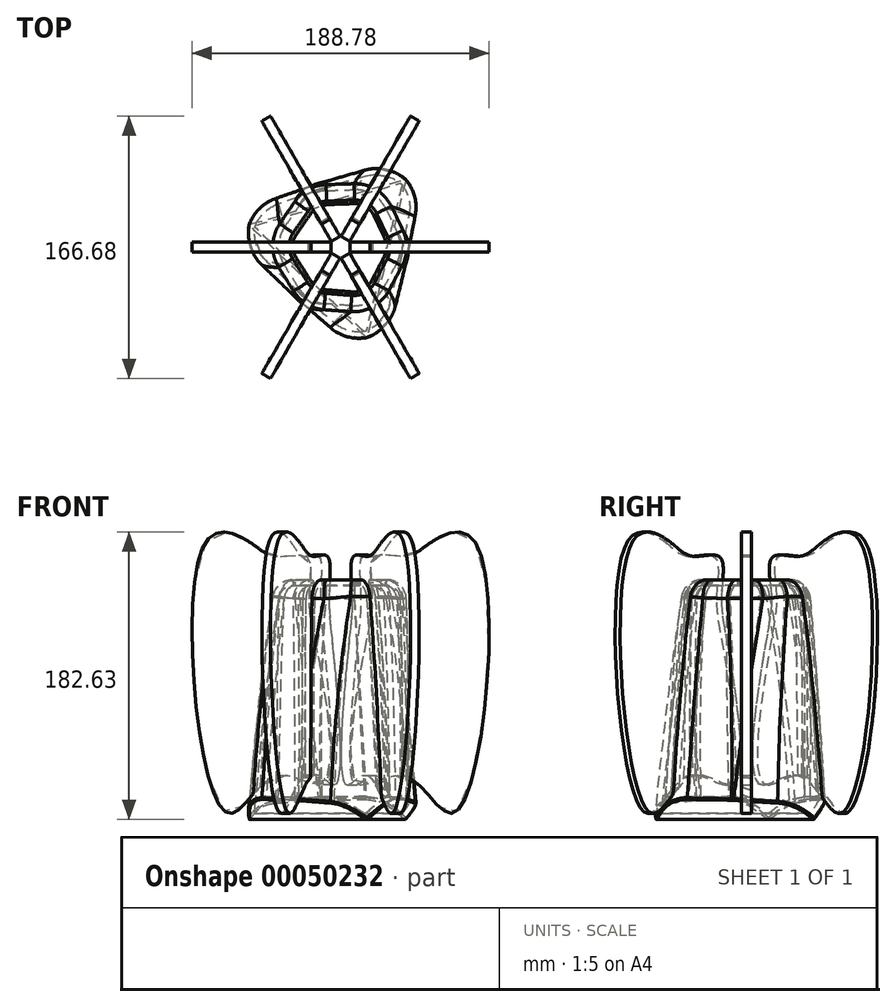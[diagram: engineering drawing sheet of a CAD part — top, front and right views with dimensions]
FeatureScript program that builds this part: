
annotation { "Feature Type Name" : "Feature", "Feature Type Description" : "" }
export const myFeature = defineFeature(function(context is Context, id is Id, definition is map)
    precondition{}
    {
        {
            var Q0;
            Q0=qCreatedBy(makeId("Top.planeOp"),FACE);
            var sketch = newSketch(context, id + "F0", { "sketchPlane" : qUnion([Q0])});
            skCircle(sketch, "E0.cCircle", {"center": v(0, 0) * mm, "radius": 42.63 * mm, "construction": true});
            skLineSegment(sketch, "E0.0", {"start": v(58, 62.5) * mm, "end": v(41.56, -9.5) * mm});
            skLineSegment(sketch, "E0.1", {"start": v(25.12, -81.48) * mm, "end": v(-29, -31.25) * mm});
            skLineSegment(sketch, "E0.2", {"start": v(-83.12, 18.99) * mm, "end": v(-12.56, 40.74) * mm});
            skPoint(sketch, "E0.0.midPoint", {"position": v(41.56, -9.5) * mm});
            skLineSegment(sketch, "E1", {"start": v(-29, -31.25) * mm, "end": v(-83.12, 18.99) * mm});
            skLineSegment(sketch, "E2", {"start": v(-12.56, 40.74) * mm, "end": v(58, 62.5) * mm});
            skLineSegment(sketch, "E3", {"start": v(41.56, -9.5) * mm, "end": v(25.12, -81.48) * mm});
            skSolve(sketch);
        }
        {
            var Q0;
            Q0=qCreatedBy(makeId("Top.planeOp"),FACE);
            cPlane(context, id + "F1", {"entities" : qUnion([Q0]), "cplaneType" : CPlaneType.OFFSET, "offset" : 152.4 * mm, "width" : 152.4 * mm, "height" : 152.4 * mm});
        }
        {
            var Q0;
            Q0=qCreatedBy(id+"F1.planeOp",FACE);
            var sketch = newSketch(context, id + "F2", { "sketchPlane" : qUnion([Q0])});
            skCircle(sketch, "E4.cCircle", {"center": v(0, 0) * mm, "radius": 39.17 * mm, "construction": true});
            skLineSegment(sketch, "E4.0", {"start": v(-22.61, 39.17) * mm, "end": v(22.61, 39.17) * mm});
            skLineSegment(sketch, "E4.1", {"start": v(22.61, 39.17) * mm, "end": v(45.23, 0) * mm});
            skLineSegment(sketch, "E4.2", {"start": v(45.23, 0) * mm, "end": v(22.61, -39.17) * mm});
            skLineSegment(sketch, "E4.3", {"start": v(22.61, -39.17) * mm, "end": v(-22.61, -39.17) * mm});
            skLineSegment(sketch, "E4.4", {"start": v(-22.61, -39.17) * mm, "end": v(-45.23, 0) * mm});
            skLineSegment(sketch, "E4.5", {"start": v(-45.23, 0) * mm, "end": v(-22.61, 39.17) * mm});
            skPoint(sketch, "E4.0.midPoint", {"position": v(0, 39.17) * mm});
            skSolve(sketch);
        }
        {
            var Q0;
            Q0=makeQuery(id+"F2.imprint","IMPRINT",FACE,{"disambiguationData":[TD([[makeQuery(id+"F2.imprint","IMPRINT",EDGE,{"derivedFrom":sQuery(id+"F2.wireOp",EDGE,"E4.0")}),-1.0]])]});
            var Q1;
            Q1=makeQuery(id+"F0.imprint","IMPRINT",FACE,{"disambiguationData":[TD([[makeQuery(id+"F0.imprint","IMPRINT",EDGE,{"derivedFrom":sQuery(id+"F0.wireOp",EDGE,"E0.0")}),-1.0]])]});
            loft(context, id + "F3", {"sheetProfilesArray" : [{ "sheetProfileEntities" : qUnion([Q0]) }, { "sheetProfileEntities" : qUnion([Q1]) }]});
        }
        {
            var Q0;
            Q0=makeQuery(id+"F3.opLoft","MID_CAP_EDGE",EDGE,{"disambiguationData":[OSD([sQuery(id+"F2.wireOp",EDGE,"E4.2"),sQuery(id+"F2.wireOp",EDGE,"E4.3"),sQuery(id+"F2.wireOp",EDGE,"E4.4")])],"capPos":0.0});
            var Q1;
            Q1=makeQuery(id+"F3.opLoft","MID_CAP_EDGE",EDGE,{"disambiguationData":[OSD([sQuery(id+"F2.wireOp",EDGE,"E4.1"),sQuery(id+"F2.wireOp",EDGE,"E4.2"),sQuery(id+"F2.wireOp",EDGE,"E4.3")])],"capPos":0.0});
            var Q2;
            Q2=makeQuery(id+"F3.opLoft","MID_CAP_EDGE",EDGE,{"disambiguationData":[OSD([sQuery(id+"F2.wireOp",EDGE,"E4.0"),sQuery(id+"F2.wireOp",EDGE,"E4.1"),sQuery(id+"F2.wireOp",EDGE,"E4.2")])],"capPos":0.0});
            var Q3;
            Q3=makeQuery(id+"F3.opLoft","MID_CAP_EDGE",EDGE,{"disambiguationData":[OSD([sQuery(id+"F2.wireOp",EDGE,"E4.0"),sQuery(id+"F2.wireOp",EDGE,"E4.1"),sQuery(id+"F2.wireOp",EDGE,"E4.5")])],"capPos":0.0});
            var Q4;
            Q4=makeQuery(id+"F3.opLoft","MID_CAP_EDGE",EDGE,{"disambiguationData":[OSD([sQuery(id+"F2.wireOp",EDGE,"E4.0"),sQuery(id+"F2.wireOp",EDGE,"E4.4"),sQuery(id+"F2.wireOp",EDGE,"E4.5")])],"capPos":0.0});
            var Q5;
            Q5=makeQuery(id+"F3.opLoft","MID_CAP_EDGE",EDGE,{"disambiguationData":[OSD([sQuery(id+"F2.wireOp",EDGE,"E4.3"),sQuery(id+"F2.wireOp",EDGE,"E4.4"),sQuery(id+"F2.wireOp",EDGE,"E4.5")])],"capPos":0.0});
            fillet(context, id + "F4", {"entities" : qUnion([Q0, Q1, Q2, Q3, Q4, Q5]), "radius" : 12.7 * mm, "tangentPropagation" : true, "allowEdgeOverflow" : false});
        }
        {
            var Q0;
            Q0=makeQuery(id+"F3.opLoft","MID_CAP_EDGE",EDGE,{"disambiguationData":[OSD([sQuery(id+"F0.wireOp",EDGE,"E0.0"),sQuery(id+"F0.wireOp",EDGE,"E0.1"),sQuery(id+"F0.wireOp",EDGE,"E3")])],"capPos":1.0});
            chamfer(context, id + "F5", {"entities" : qUnion([Q0]), "width" : 12.7 * mm, "tangentPropagation" : true});
        }
        {
            var Q0;
            Q0=makeQuery(id+"F3.opLoft","MID_CAP_EDGE",EDGE,{"disambiguationData":[OSD([sQuery(id+"F0.wireOp",EDGE,"E0.0"),sQuery(id+"F0.wireOp",EDGE,"E0.2"),sQuery(id+"F0.wireOp",EDGE,"E2")])],"capPos":1.0});
            chamfer(context, id + "F6", {"entities" : qUnion([Q0]), "width" : 12.7 * mm, "tangentPropagation" : true});
        }
        {
            var Q0;
            Q0=makeQuery(id+"F3.opLoft","MID_CAP_EDGE",EDGE,{"disambiguationData":[OSD([sQuery(id+"F0.wireOp",EDGE,"E0.1"),sQuery(id+"F0.wireOp",EDGE,"E0.2"),sQuery(id+"F0.wireOp",EDGE,"E1")])],"capPos":1.0});
            chamfer(context, id + "F7", {"entities" : qUnion([Q0]), "width" : 12.7 * mm, "tangentPropagation" : true});
        }
        {
            var Q0;
            Q0=makeQuery(id+"F3.opLoft","SWEPT_EDGE",EDGE,{"disambiguationData":[OSD([sQuery(id+"F0.wireOp",EDGE,"E0.1"),sQuery(id+"F0.wireOp",EDGE,"E3"),sQuery(id+"F2.wireOp",EDGE,"E4.2"),sQuery(id+"F2.wireOp",EDGE,"E4.3")])]});
            var Q1;
            Q1=makeQuery(id+"F3.opLoft","SWEPT_EDGE",EDGE,{"disambiguationData":[OSD([sQuery(id+"F0.wireOp",EDGE,"E0.0"),sQuery(id+"F0.wireOp",EDGE,"E3"),sQuery(id+"F2.wireOp",EDGE,"E4.1"),sQuery(id+"F2.wireOp",EDGE,"E4.2")])]});
            var Q2;
            Q2=makeQuery(id+"F3.opLoft","SWEPT_EDGE",EDGE,{"disambiguationData":[OSD([sQuery(id+"F0.wireOp",EDGE,"E0.0"),sQuery(id+"F0.wireOp",EDGE,"E2"),sQuery(id+"F2.wireOp",EDGE,"E4.0"),sQuery(id+"F2.wireOp",EDGE,"E4.1")])]});
            var Q3;
            Q3=makeQuery(id+"F3.opLoft","SWEPT_EDGE",EDGE,{"disambiguationData":[OSD([sQuery(id+"F0.wireOp",EDGE,"E0.2"),sQuery(id+"F0.wireOp",EDGE,"E2"),sQuery(id+"F2.wireOp",EDGE,"E4.0"),sQuery(id+"F2.wireOp",EDGE,"E4.5")])]});
            var Q4;
            Q4=makeQuery(id+"F3.opLoft","SWEPT_EDGE",EDGE,{"disambiguationData":[OSD([sQuery(id+"F0.wireOp",EDGE,"E0.2"),sQuery(id+"F0.wireOp",EDGE,"E1"),sQuery(id+"F2.wireOp",EDGE,"E4.4"),sQuery(id+"F2.wireOp",EDGE,"E4.5")])]});
            var Q5;
            Q5=makeQuery(id+"F3.opLoft","SWEPT_EDGE",EDGE,{"disambiguationData":[OSD([sQuery(id+"F0.wireOp",EDGE,"E0.1"),sQuery(id+"F0.wireOp",EDGE,"E1"),sQuery(id+"F2.wireOp",EDGE,"E4.3"),sQuery(id+"F2.wireOp",EDGE,"E4.4")])]});
            fillet(context, id + "F8", {"entities" : qUnion([Q0, Q1, Q2, Q3, Q4, Q5]), "radius" : 25.4 * mm, "tangentPropagation" : true, "allowEdgeOverflow" : false});
        }
        {
            var Q0;
            Q0=makeQuery(id+"F3.opLoft","CAP_FACE",FACE,{"disambiguationData":[OSD([makeQuery(id+"F2.imprint","IMPRINT",FACE,{"disambiguationData":[TD([[makeQuery(id+"F2.imprint","IMPRINT",EDGE,{"derivedFrom":sQuery(id+"F2.wireOp",EDGE,"E4.0")}),-1.0]])]})])],"isStart":true});
            shell(context, id + "F9", {"entities" : qUnion([Q0]), "thickness" : 3.8 * mm});
        }
        {
            var Q0;
            {var subQ0=sQuery(id+"F2.wireOp",EDGE,"E4.0");var subQ1=sQuery(id+"F2.wireOp",EDGE,"E4.4");var subQ2=sQuery(id+"F2.wireOp",EDGE,"E4.5");Q0=makeQuery(id+"F4.opFillet","BLEND_EDGE",EDGE,{"blendedFrom":[makeQuery(id+"F3.opLoft","MID_CAP_EDGE",EDGE,{"disambiguationData":[OSD([subQ0,subQ1,subQ2])],"capPos":0.0}),makeQuery(id+"F3.opLoft","CAP_FACE",FACE,{"disambiguationData":[OSD([makeQuery(id+"F2.imprint","IMPRINT",FACE,{"disambiguationData":[TD([[makeQuery(id+"F2.imprint","IMPRINT",EDGE,{"derivedFrom":subQ0}),-1.0]])]})])],"isStart":true})],"blendedInto":[makeQuery(id+"F3.opLoft","CAP_FACE",FACE,{"disambiguationData":[OSD([makeQuery(id+"F2.imprint","IMPRINT",FACE,{"disambiguationData":[TD([[makeQuery(id+"F2.imprint","IMPRINT",EDGE,{"derivedFrom":subQ0}),-1.0]])]})])],"isStart":true})]});}
            var Q1;
            {var subQ0=sQuery(id+"F2.wireOp",EDGE,"E4.1");var subQ1=sQuery(id+"F2.wireOp",EDGE,"E4.0");var subQ2=sQuery(id+"F2.wireOp",EDGE,"E4.4");var subQ3=sQuery(id+"F2.wireOp",EDGE,"E4.5");Q1=makeQuery(id+"F8.opFillet","BLEND_EDGE",EDGE,{"blendedFrom":[makeQuery(id+"F4.opFillet","BLEND_EDGE",EDGE,{"blendedFrom":[makeQuery(id+"F3.opLoft","MID_CAP_EDGE",EDGE,{"disambiguationData":[OSD([subQ1,subQ0,subQ3])],"capPos":0.0}),makeQuery(id+"F3.opLoft","MID_CAP_EDGE",EDGE,{"disambiguationData":[OSD([subQ1,subQ2,subQ3])],"capPos":0.0})],"blendedInto":[]}),makeQuery(id+"F3.opLoft","CAP_FACE",FACE,{"disambiguationData":[OSD([makeQuery(id+"F2.imprint","IMPRINT",FACE,{"disambiguationData":[TD([[makeQuery(id+"F2.imprint","IMPRINT",EDGE,{"derivedFrom":subQ1}),-1.0]])]})])],"isStart":true})],"blendedInto":[makeQuery(id+"F3.opLoft","CAP_FACE",FACE,{"disambiguationData":[OSD([makeQuery(id+"F2.imprint","IMPRINT",FACE,{"disambiguationData":[TD([[makeQuery(id+"F2.imprint","IMPRINT",EDGE,{"derivedFrom":subQ1}),-1.0]])]})])],"isStart":true})]});}
            fillet(context, id + "F10", {"entities" : qUnion([Q0, Q1]), "radius" : 1.9 * mm, "tangentPropagation" : true, "allowEdgeOverflow" : false});
        }
        {
            var Q0;
            {var subQ0=sQuery(id+"F0.wireOp",EDGE,"E3");var subQ1=sQuery(id+"F0.wireOp",EDGE,"E0.1");var subQ2=sQuery(id+"F0.wireOp",EDGE,"E0.0");Q0=makeQuery(id+"F5.opChamfer","BLEND_EDGE",EDGE,{"blendedFrom":[makeQuery(id+"F3.opLoft","MID_CAP_EDGE",EDGE,{"disambiguationData":[OSD([subQ2,subQ1,subQ0])],"capPos":1.0}),makeQuery(id+"F3.opLoft","SWEPT_FACE",FACE,{"disambiguationData":[OSD([subQ2,subQ1,subQ0,sQuery(id+"F2.wireOp",EDGE,"E4.1"),sQuery(id+"F2.wireOp",EDGE,"E4.2"),sQuery(id+"F2.wireOp",EDGE,"E4.3")])]})],"blendedInto":[makeQuery(id+"F3.opLoft","SWEPT_FACE",FACE,{"disambiguationData":[OSD([subQ2,subQ1,subQ0,sQuery(id+"F2.wireOp",EDGE,"E4.1"),sQuery(id+"F2.wireOp",EDGE,"E4.2"),sQuery(id+"F2.wireOp",EDGE,"E4.3")])]})]});}
            var Q1;
            {var subQ0=sQuery(id+"F0.wireOp",EDGE,"E2");var subQ1=sQuery(id+"F0.wireOp",EDGE,"E0.0");Q1=makeQuery(id+"F8.opFillet","BLEND_EDGE",EDGE,{"blendedFrom":[makeQuery(id+"F3.opLoft","SWEPT_EDGE",EDGE,{"disambiguationData":[OSD([subQ1,subQ0,sQuery(id+"F2.wireOp",EDGE,"E4.0"),sQuery(id+"F2.wireOp",EDGE,"E4.1")])]}),makeQuery(id+"F6.opChamfer","BLEND_FACE",FACE,{"disambiguationData":[OSD([subQ1,sQuery(id+"F0.wireOp",EDGE,"E0.2"),subQ0])]})],"blendedInto":[makeQuery(id+"F6.opChamfer","BLEND_FACE",FACE,{"disambiguationData":[OSD([subQ1,sQuery(id+"F0.wireOp",EDGE,"E0.2"),subQ0])]})]});}
            var Q2;
            {var subQ0=sQuery(id+"F0.wireOp",EDGE,"E1");var subQ1=sQuery(id+"F0.wireOp",EDGE,"E0.2");Q2=makeQuery(id+"F8.opFillet","BLEND_EDGE",EDGE,{"blendedFrom":[makeQuery(id+"F3.opLoft","SWEPT_EDGE",EDGE,{"disambiguationData":[OSD([subQ1,subQ0,sQuery(id+"F2.wireOp",EDGE,"E4.4"),sQuery(id+"F2.wireOp",EDGE,"E4.5")])]}),makeQuery(id+"F7.opChamfer","BLEND_FACE",FACE,{"disambiguationData":[OSD([sQuery(id+"F0.wireOp",EDGE,"E0.1"),subQ1,subQ0])]})],"blendedInto":[makeQuery(id+"F7.opChamfer","BLEND_FACE",FACE,{"disambiguationData":[OSD([sQuery(id+"F0.wireOp",EDGE,"E0.1"),subQ1,subQ0])]})]});}
            fillet(context, id + "F11", {"entities" : qUnion([Q0, Q1, Q2]), "radius" : 1.27 * mm, "tangentPropagation" : true, "allowEdgeOverflow" : false});
        }
        {
            var Q0;
            Q0=qCreatedBy(makeId("Front.planeOp"),FACE);
            var sketch = newSketch(context, id + "F12", { "sketchPlane" : qUnion([Q0])});
            skFitSpline(sketch, "E5", {"points": [v(-58.59, 176.75) * mm, v(-40.94, 167.2) * mm, v(-21, 166.47) * mm, v(-20.02, 144.12) * mm, v(-15.74, 110.88) * mm, v(-10.7, 22.84) * mm, v(-41.2, 27.5) * mm, v(-72.48, 4.3) * mm, v(-85.79, 175.88) * mm, v(-58.59, 176.75) * mm]});
            skLineSegment(sketch, "E6", {"start": v(0, 0) * mm, "end": v(0, 80.04) * mm});
            skSolve(sketch);
        }
        {
            var Q0;
            Q0=makeQuery(id+"F12.imprint","IMPRINT",FACE,{"disambiguationData":[TD([[makeQuery(id+"F12.imprint","IMPRINT",EDGE,{"derivedFrom":sQuery(id+"F12.wireOp",EDGE,"E5")}),-1.0]])]});
            extrude(context, id + "F13", {"entities" : qUnion([Q0]), "endBound" : BoundingType.SYMMETRIC, "depth" : 6.35 * mm});
        }
        {
            var Q0;
            Q0=makeQuery(id+"F13.opExtrude","SWEPT_BODY",BODY,{"disambiguationData":[OSD([sQuery(id+"F12.wireOp",EDGE,"E5")])]});
            var Q1;
            Q1=sQuery(id+"F12.wireOp",EDGE,"E6");
            circularPattern(context, id + "F14", {"entities" : qUnion([Q0]), "axis" : qUnion([Q1]), "angle" : 360 * degree, "instanceCount" : 6, "equalSpace" : true});
        }
        {
            var Q0;
            Q0=makeQuery(id+"F14.opPattern","COPY",BODY,{"derivedFrom":makeQuery(id+"F13.opExtrude","SWEPT_BODY",BODY,{"disambiguationData":[OSD([sQuery(id+"F12.wireOp",EDGE,"E5")])]}),"instanceName":"1"});
            var Q1;
            Q1=makeQuery(id+"F13.opExtrude","SWEPT_BODY",BODY,{"disambiguationData":[OSD([sQuery(id+"F12.wireOp",EDGE,"E5")])]});
            var Q2;
            Q2=makeQuery(id+"F14.opPattern","COPY",BODY,{"derivedFrom":makeQuery(id+"F13.opExtrude","SWEPT_BODY",BODY,{"disambiguationData":[OSD([sQuery(id+"F12.wireOp",EDGE,"E5")])]}),"instanceName":"5"});
            var Q3;
            Q3=makeQuery(id+"F14.opPattern","COPY",BODY,{"derivedFrom":makeQuery(id+"F13.opExtrude","SWEPT_BODY",BODY,{"disambiguationData":[OSD([sQuery(id+"F12.wireOp",EDGE,"E5")])]}),"instanceName":"4"});
            var Q4;
            Q4=makeQuery(id+"F14.opPattern","COPY",BODY,{"derivedFrom":makeQuery(id+"F13.opExtrude","SWEPT_BODY",BODY,{"disambiguationData":[OSD([sQuery(id+"F12.wireOp",EDGE,"E5")])]}),"instanceName":"3"});
            var Q5;
            Q5=makeQuery(id+"F14.opPattern","COPY",BODY,{"derivedFrom":makeQuery(id+"F13.opExtrude","SWEPT_BODY",BODY,{"disambiguationData":[OSD([sQuery(id+"F12.wireOp",EDGE,"E5")])]}),"instanceName":"2"});
            var Q6;
            Q6=makeQuery(id+"F3.opLoft","SWEPT_BODY",BODY,{"disambiguationData":[OSD([makeQuery(id+"F0.imprint","IMPRINT",FACE,{"disambiguationData":[TD([[makeQuery(id+"F0.imprint","IMPRINT",EDGE,{"derivedFrom":sQuery(id+"F0.wireOp",EDGE,"E0.0")}),-1.0]])]}),makeQuery(id+"F2.imprint","IMPRINT",FACE,{"disambiguationData":[TD([[makeQuery(id+"F2.imprint","IMPRINT",EDGE,{"derivedFrom":sQuery(id+"F2.wireOp",EDGE,"E4.0")}),-1.0]])]})])]});
            booleanBodies(context, id + "F15", {"operationType" : BooleanOperationType.SUBTRACTION, "tools" : qUnion([Q0, Q1, Q2, Q3, Q4, Q5]), "targets" : qUnion([Q6]), "keepTools" : true});
        }
    });
